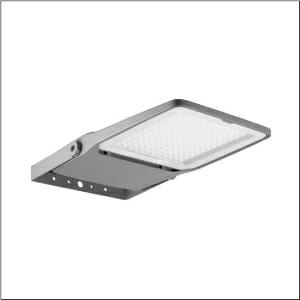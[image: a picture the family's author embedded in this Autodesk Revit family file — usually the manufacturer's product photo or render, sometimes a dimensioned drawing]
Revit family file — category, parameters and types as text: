
# Revit family: floodlight_fl_20_midi___pl43_5xa7682e2a2ac_5f4f
name_source: partatom
category: Lighting Fixtures
units: mm (PartAtom-declared; Revit-internal decimal feet)

## family parameters
Cut with Voids When Loaded = No
Host = Face
Light Source = No
Part Type = Normal
Room Calculation Point = No
Round Connector Dimension = Use Diameter
Shared = No

## types (1)
- --- (1 x LED 4000K / CRI = 70 (unbekannt), 28460 lm, 4000K)
    Apparent Load = 208 VA
    CIE Flux Codes = 32 74 99 100 100
    Color Rendering = 70
    Color Temperature = 4000K
    Default Elevation = 1800 mm
    Description = Floodlight FL 20 midi, floodlight, primary light control with lens, of plastic, primary optical cover: protective disc, of toughened safety glass, transparent, light distribution: PL43, light emission: direct distribution, primary light characteristic: asymmetric, installation type: surface-mounted, LED, High Power LED, rated luminous flux: 28.460lm, luminous efficacy: 137lm/W, light colour: 740, colour temperature: 4000K, control gear: ECG Plus, control: flexible luminous flux parameterisation, time-dependent luminous flux control, digital communication interface, power reduction, overheat protection, electronic power reduction, with terminal, 5-pole, max. 2.5mm², mains connection: 220..240V, AC, 50/60Hz, rated input power: 208W, LED unit, of diecast aluminium, powder-coated, Siteco® metallic grey (DB 702S), corrosivity category C5 mid according to DIN EN ISO 12944, incl. 1x M20 cable gland for cable Ø 6.5..12mm, length: 731mm, width: 450mm, height: 76mm, housing frame, of diecast aluminium, powder-coated, Siteco® metallic grey (DB 702S), wall fastening, of steel, powder-coated, Siteco® metallic grey (DB 702S), DALI, protection rating (complete): IP66, insulation class (complete): insulation class II (safety insulation), certification: CE, ENEC, VDE, protection symbol: D, permissible operating ambient temperature: -40..+40°C, permissible operating ambient temperature for outdoor applications: -40..+50°C, standard: DIN EN 12944, packaging unit: 1 piece

Light Distribution: PL43
    Height = 76 mm
    Lamp = 1 x LED 4000K / CRI >= 70 (unbekannt)
    Lamp Light Flux = 28460 lm
    Lamp count = 1
    Length = 731 mm
    Luminous efficacy = 137 lm/W
    Manufacturer = Siteco
    ModVariant = No
    Model = 5XA7682E2A2AC
    Mounting Place = Wall
    Mounting Type = Surface mounted
    Number of Poles = 1
    OnlyDefault = Yes
    Power Factor = 1
    Product Name = Floodlight FL 20 midi | PL43
    Product group = floodlight | wall mounted
    ProductGroupID = 2001
    Protection Class = Protection class II
    Protection Degree = IP 66
    RLX_Detail_Level = 1
    RLX_Emergency_Light_Flux = 0 lm
    RLX_Emergency_Type = 0
    RLX_Emergency_Type_DB = No
    RlxData = <blob elided: 92081 chars, md5=e29b37cc>
    Socket = socket
    Standby Power = 0 W
    System Light Flux = 28460 lm
    System Power = 208 W
    Type Comments = factory setting: luminous flux: 100 % | dim-lin: 254 | 484 mA
    Type Image = l_1005944.jpg
    URL = http://relux.com
    VarID = @adj_148293
    Voltage = 0 V
    Weight = 0.00 kg
    Width = 450 mm

## geometry (parser evidence)
native form markers: Blend x4, Sweep x11
no freeform markers — native parametric forms only
